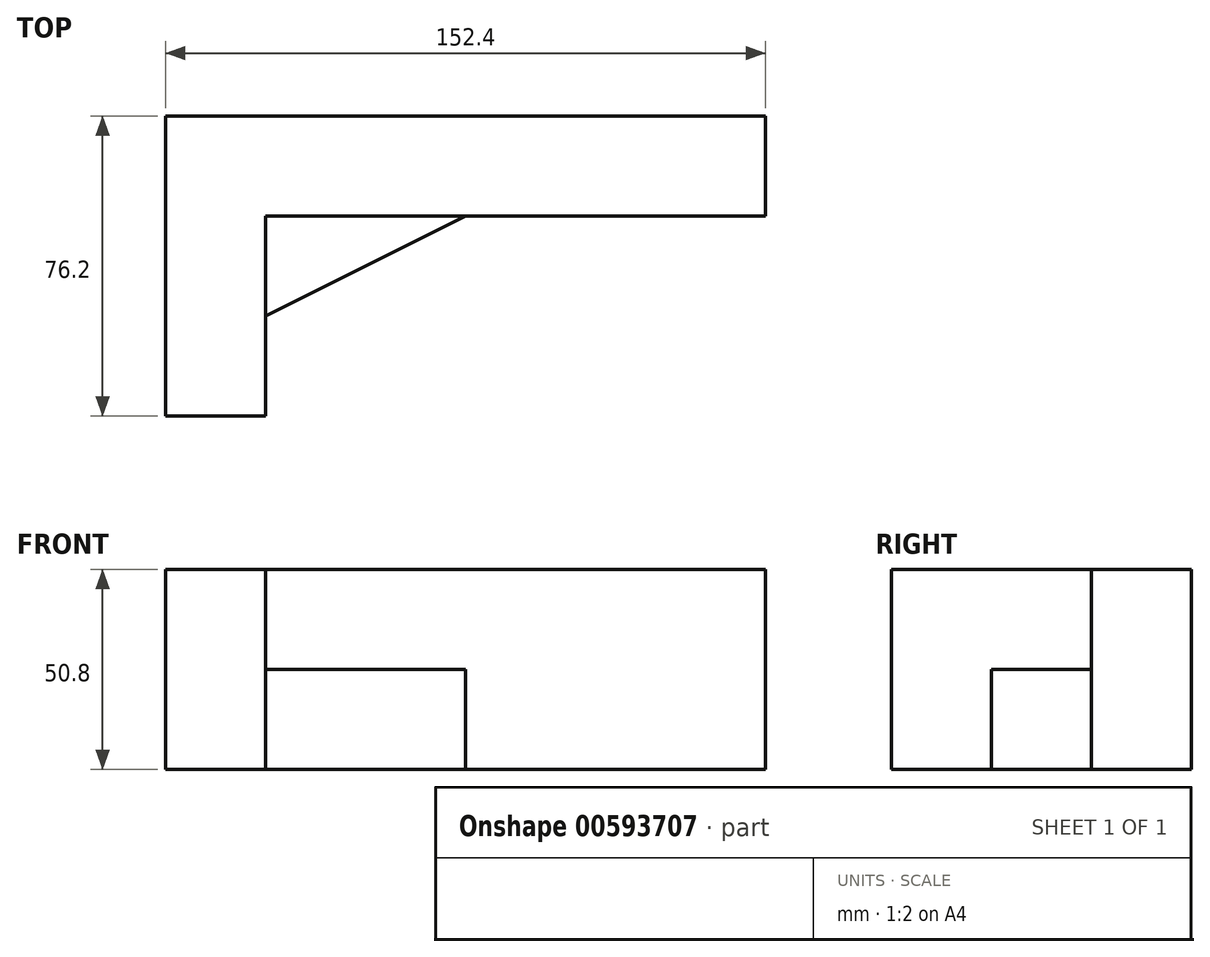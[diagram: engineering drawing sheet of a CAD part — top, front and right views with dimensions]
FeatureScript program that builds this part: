
annotation { "Feature Type Name" : "Feature", "Feature Type Description" : "" }
export const myFeature = defineFeature(function(context is Context, id is Id, definition is map)
    precondition{}
    {
        {
            var Q0;
            Q0=qCreatedBy(makeId("Top.planeOp"),FACE);
            var sketch = newSketch(context, id + "F0", { "sketchPlane" : qUnion([Q0])});
            skLineSegment(sketch, "E0", {"start": v(0, 0) * mm, "end": v(0, 76.2) * mm});
            skLineSegment(sketch, "E1", {"start": v(0, 76.2) * mm, "end": v(152.4, 76.2) * mm});
            skLineSegment(sketch, "E2", {"start": v(152.4, 76.2) * mm, "end": v(152.4, 50.8) * mm});
            skLineSegment(sketch, "E3", {"start": v(152.4, 50.8) * mm, "end": v(25.4, 50.8) * mm});
            skLineSegment(sketch, "E4", {"start": v(25.4, 50.8) * mm, "end": v(25.4, 0) * mm});
            skLineSegment(sketch, "E5", {"start": v(25.4, 0) * mm, "end": v(0, 0) * mm});
            skLineSegment(sketch, "E6", {"start": v(76.2, 50.8) * mm, "end": v(25.4, 25.4) * mm});
            skSolve(sketch);
        }
        {
            var Q0;
            Q0 = qSketchRegion(id + "F0", true);
            extrude(context, id + "F1", {"entities" : qUnion([Q0]), "depth" : 50.8 * mm, "offsetDistance" : 25.4 * mm});
        }
        {
            var Q0;
            Q0=makeQuery(id+"F1.opExtrude","CAP_FACE",FACE,{"disambiguationData":[OSD([sQuery(id+"F0.wireOp",EDGE,"E0"),sQuery(id+"F0.wireOp",EDGE,"E1"),sQuery(id+"F0.wireOp",EDGE,"E2"),sQuery(id+"F0.wireOp",EDGE,"E3"),sQuery(id+"F0.wireOp",EDGE,"E4"),sQuery(id+"F0.wireOp",EDGE,"E5"),sQuery(id+"F0.wireOp",EDGE,"E6")])],"isStart":false});
            var sketch = newSketch(context, id + "F2", { "sketchPlane" : qUnion([Q0])});
            skLineSegment(sketch, "E7", {"start": v(25.4, 25.4) * mm, "end": v(25.4, 50.8) * mm});
            skLineSegment(sketch, "E8", {"start": v(25.4, 50.8) * mm, "end": v(76.2, 50.8) * mm});
            skSolve(sketch);
        }
        {
            var Q0;
            Q0 = qSketchRegion(id + "F2", true);
            var Q1;
            Q1=makeQuery(id+"F2.imprint","IMPRINT",FACE,{"disambiguationData":[TD([[makeQuery(id+"F2.imprint","IMPRINT",EDGE,{"derivedFrom":sQuery(id+"F2.wireOp",EDGE,"E7")}),-1.0]])]});
            extrude(context, id + "F3", {"entities" : qUnion([Q0, Q1]), "operationType" : NewBodyOperationType.REMOVE, "oppositeDirection" : true, "depth" : 25.4 * mm, "offsetDistance" : 25.4 * mm});
        }
    });
